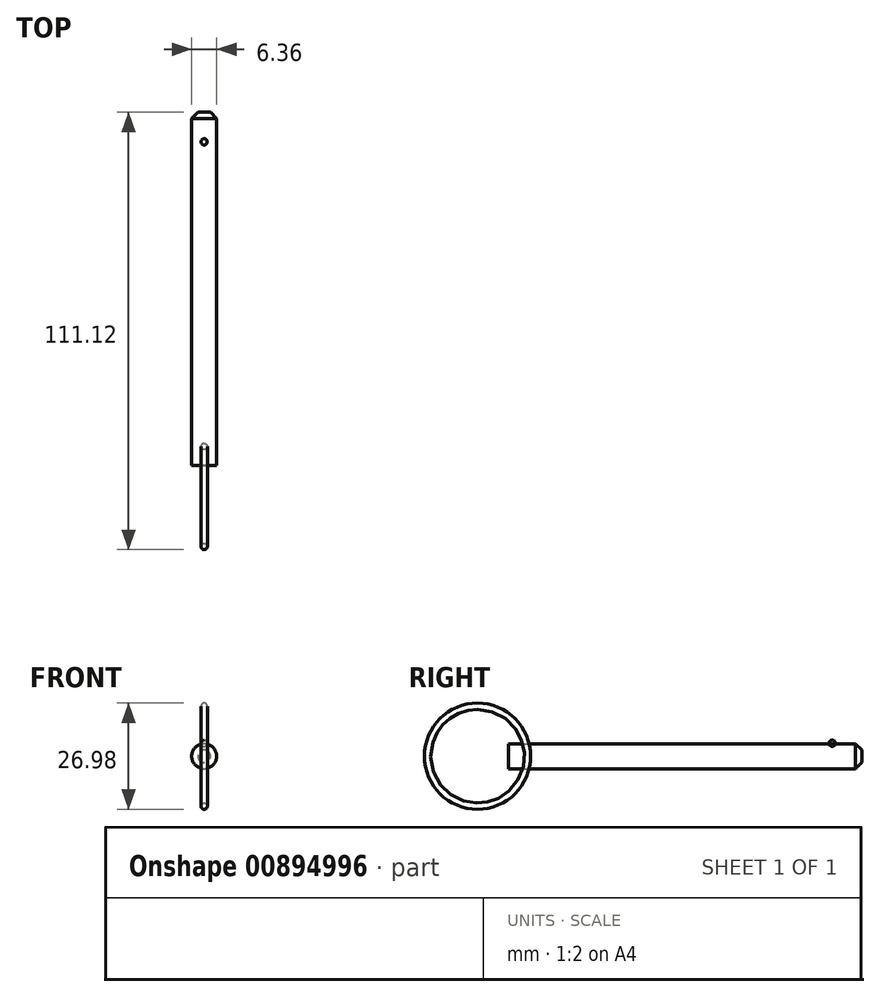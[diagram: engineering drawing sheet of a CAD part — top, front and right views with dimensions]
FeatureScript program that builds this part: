
annotation { "Feature Type Name" : "Feature", "Feature Type Description" : "" }
export const myFeature = defineFeature(function(context is Context, id is Id, definition is map)
    precondition{}
    {
        {
            var Q0;
            Q0=qCreatedBy(makeId("Front.planeOp"),FACE);
            var sketch = newSketch(context, id + "F0", { "sketchPlane" : qUnion([Q0])});
            skCircle(sketch, "E0", {"center": v(0, 0) * mm, "radius": 3.18 * mm});
            skSolve(sketch);
        }
        {
            var Q0;
            Q0 = qSketchRegion(id + "F0", true);
            extrude(context, id + "F1", {"entities" : qUnion([Q0]), "endBound" : BoundingType.SYMMETRIC, "depth" : 89.7 * mm, "offsetDistance" : 25.4 * mm});
        }
        {
            var Q0;
            Q0=makeQuery(id+"F1.opExtrude","CAP_EDGE",EDGE,{"disambiguationData":[OSD([sQuery(id+"F0.wireOp",EDGE,"E0")])],"isStart":true});
            chamfer(context, id + "F2", {"entities" : qUnion([Q0]), "width" : 1.59 * mm, "tangentPropagation" : true});
        }
        {
            var Q0;
            Q0=qCreatedBy(makeId("Right.planeOp"),FACE);
            var sketch = newSketch(context, id + "F3", { "sketchPlane" : qUnion([Q0])});
            skArc(sketch, "E1", {"start": v(37.35, 2.5) * mm, "mid": v(38.14, 3.3) * mm, "end": v(37.35, 4.09) * mm});
            skLineSegment(sketch, "E2", {"start": v(43.27, -3.18) * mm, "end": v(-44.86, -3.18) * mm, "construction": true});
            skLineSegment(sketch, "E3", {"start": v(37.35, 4.09) * mm, "end": v(37.35, 2.5) * mm});
            skLineSegment(sketch, "E4", {"start": v(37.35, 3.3) * mm, "end": v(37.35, 7.4) * mm, "construction": true});
            skSolve(sketch);
        }
        {
            var Q0;
            Q0=makeQuery(id+"F3.imprint","IMPRINT",FACE,{"disambiguationData":[TD([[makeQuery(id+"F3.imprint","IMPRINT",EDGE,{"derivedFrom":sQuery(id+"F3.wireOp",EDGE,"E1")}),1.0]])]});
            var Q1;
            Q1=sQuery(id+"F3.wireOp",EDGE,"E4");
            revolve(context, id + "F4", {"surfaceOperationType" : NewSurfaceOperationType.NEW, "entities" : qUnion([Q0]), "axis" : qUnion([Q1]), "revolveType" : RevolveType.FULL});
        }
        {
            var Q0;
            Q0=qCreatedBy(makeId("Top.planeOp"),FACE);
            var sketch = newSketch(context, id + "F5", { "sketchPlane" : qUnion([Q0])});
            skCircle(sketch, "E5", {"center": v(0, -40.06) * mm, "radius": 0.8 * mm});
            skLineSegment(sketch, "E6.0", {"start": v(3.18, -44.86) * mm, "end": v(-3.18, -44.86) * mm, "construction": true});
            skLineSegment(sketch, "E7", {"start": v(-5.77, -52.76) * mm, "end": v(16.79, -52.76) * mm, "construction": true});
            skSolve(sketch);
        }
        {
            var Q0;
            Q0=makeQuery(id+"F5.imprint","IMPRINT",FACE,{"disambiguationData":[TD([[makeQuery(id+"F5.imprint","IMPRINT",EDGE,{"derivedFrom":sQuery(id+"F5.wireOp",EDGE,"E5")}),1.0]])]});
            var Q1;
            Q1=sQuery(id+"F5.wireOp",EDGE,"E7");
            revolve(context, id + "F6", {"surfaceOperationType" : NewSurfaceOperationType.NEW, "entities" : qUnion([Q0]), "axis" : qUnion([Q1]), "revolveType" : RevolveType.FULL});
        }
    });
